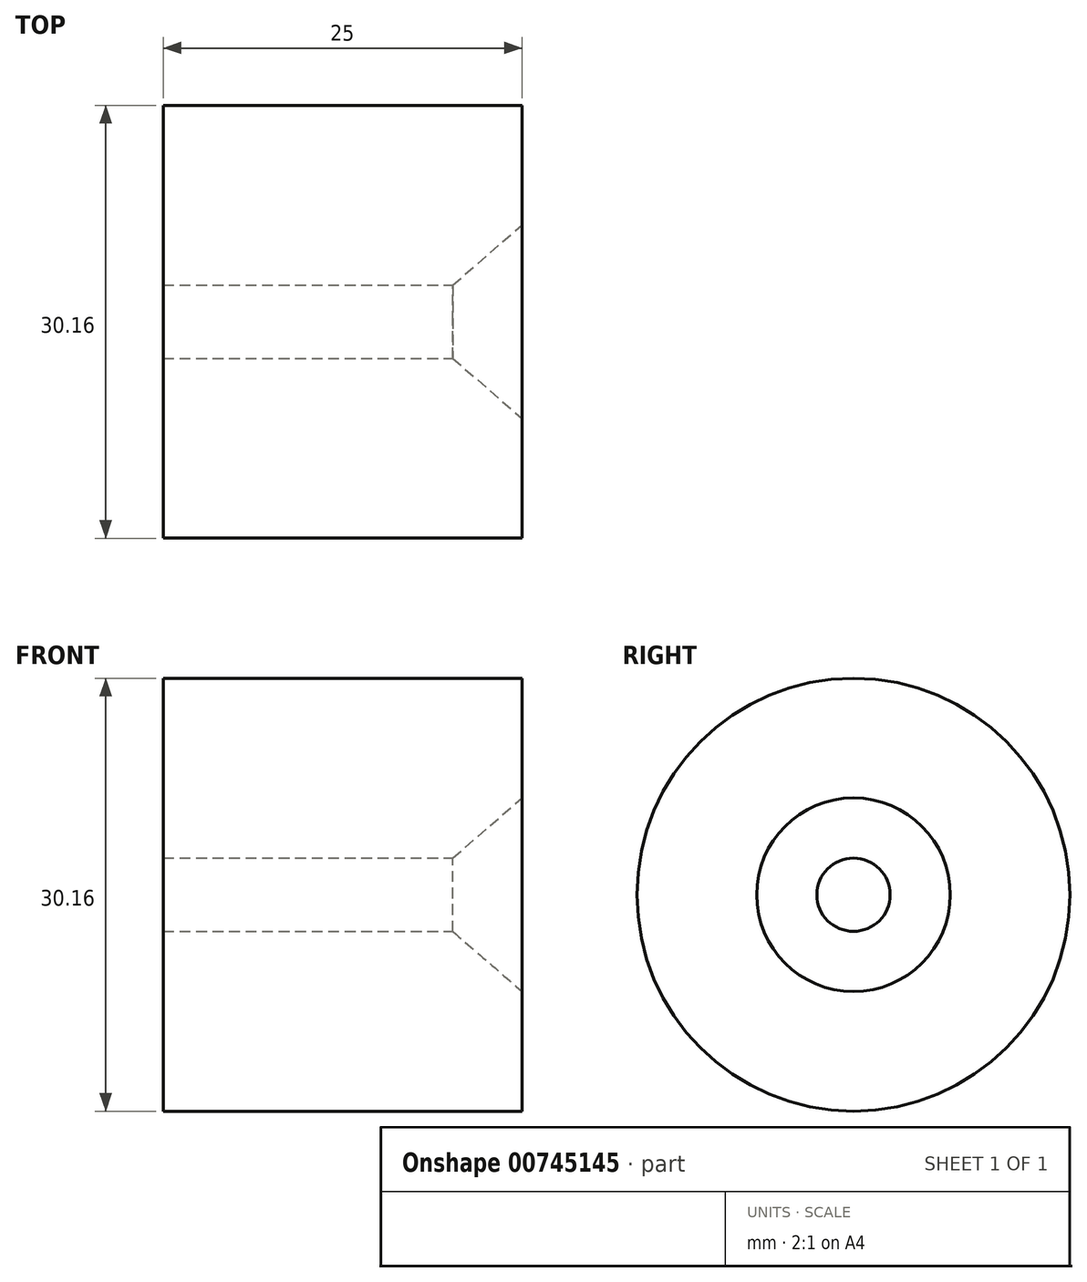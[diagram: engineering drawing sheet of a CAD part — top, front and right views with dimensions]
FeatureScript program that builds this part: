
annotation { "Feature Type Name" : "Feature", "Feature Type Description" : "" }
export const myFeature = defineFeature(function(context is Context, id is Id, definition is map)
    precondition{}
    {
        {
            var Q0;
            Q0=qCreatedBy(makeId("Right.planeOp"),FACE);
            var sketch = newSketch(context, id + "F0", { "sketchPlane" : qUnion([Q0])});
            skCircle(sketch, "E0", {"center": v(28.9, 29.04) * mm, "radius": 15.08 * mm});
            skSolve(sketch);
        }
        {
            var Q0;
            Q0 = qSketchRegion(id + "F0", true);
            extrude(context, id + "F1", {"entities" : qUnion([Q0]), "depth" : 25 * mm, "offsetDistance" : 25 * mm});
        }
        {
            var Q0;
            Q0=makeQuery(id+"F1.opExtrude","CAP_FACE",FACE,{"disambiguationData":[OSD([sQuery(id+"F0.wireOp",EDGE,"E0")])],"isStart":false});
            var sketch = newSketch(context, id + "F2", { "sketchPlane" : qUnion([Q0])});
            skPoint(sketch, "E1", {"position": v(28.9, 29.04) * mm});
            skSolve(sketch);
        }
        {
            var Q0;
            Q0=sQuery(id+"F2.wireOp",VERTEX,"E1");
            var Q1;
            Q1=makeQuery(id+"F1.opExtrude","SWEPT_BODY",BODY,{"disambiguationData":[OSD([sQuery(id+"F0.wireOp",EDGE,"E0")])]});
            hole(context, id + "F3", {"style" : HoleStyle.C_SINK, "endStyle" : HoleEndStyle.THROUGH, "standardTappedOrClearance" : lookupTablePath({ "standard" : "ANSI", "engagement" : "75%", "pitch" : "20 tpi", "size" : "1/4", "type" : "Tapped" }), "standardBlindInLast" : lookupTablePath({ "standard" : "ANSI", "engagement" : "75%", "pitch" : "20 tpi", "size" : "1/4", "type" : "Tapped" }), "holeDiameter" : 5.1 * mm, "cSinkDiameter" : 13.5 * mm, "cSinkAngle" : 82 * degree, "majorDiameter" : 6.35 * mm, "showTappedDepth" : true, "isTappedThrough" : true, "tappedDepth" : 12 * mm, "tapClearance" : 3, "startFromSketch" : true, "locations" : qUnion([Q0]), "scope" : qUnion([Q1])});
        }
    });
